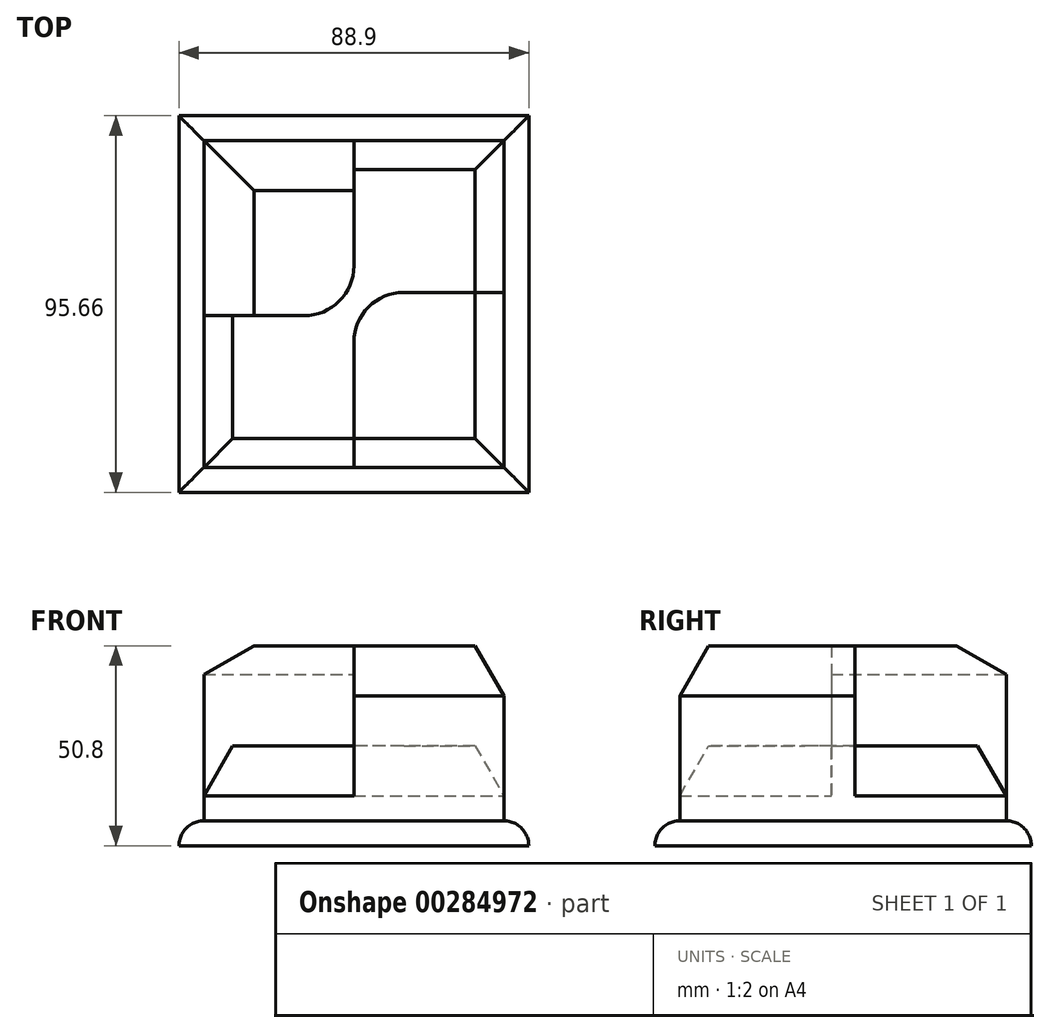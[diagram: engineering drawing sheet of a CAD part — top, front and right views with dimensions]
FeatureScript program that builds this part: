
annotation { "Feature Type Name" : "Feature", "Feature Type Description" : "" }
export const myFeature = defineFeature(function(context is Context, id is Id, definition is map)
    precondition{}
    {
        {
            var Q0;
            Q0=qCreatedBy(makeId("Top.planeOp"),FACE);
            var sketch = newSketch(context, id + "F0", { "sketchPlane" : qUnion([Q0])});
            skLineSegment(sketch, "E0.bottom", {"start": v(44.45, 47.83) * mm, "end": v(-44.45, 47.83) * mm});
            skLineSegment(sketch, "E0.top", {"start": v(44.45, -47.83) * mm, "end": v(-44.45, -47.83) * mm});
            skLineSegment(sketch, "E0.left", {"start": v(44.45, 47.83) * mm, "end": v(44.45, -47.83) * mm});
            skLineSegment(sketch, "E0.right", {"start": v(-44.45, 47.83) * mm, "end": v(-44.45, -47.83) * mm});
            skPoint(sketch, "E0.middle", {"position": v(0, 0) * mm});
            skLineSegment(sketch, "E1.0", {"start": v(38.1, 41.48) * mm, "end": v(-38.1, 41.48) * mm});
            skLineSegment(sketch, "E2.0", {"start": v(38.1, 41.48) * mm, "end": v(38.1, -41.48) * mm});
            skLineSegment(sketch, "E3.0", {"start": v(38.1, -41.48) * mm, "end": v(-38.1, -41.48) * mm});
            skLineSegment(sketch, "E4.0", {"start": v(-38.1, 41.48) * mm, "end": v(-38.1, -41.48) * mm});
            skLineSegment(sketch, "E5", {"start": v(0, 41.48) * mm, "end": v(0, 9.73) * mm});
            skLineSegment(sketch, "E6", {"start": v(-12.7, -2.97) * mm, "end": v(-38.1, -2.97) * mm});
            skLineSegment(sketch, "E7", {"start": v(0, -41.48) * mm, "end": v(0, -9.73) * mm});
            skLineSegment(sketch, "E8", {"start": v(12.7, 2.97) * mm, "end": v(38.1, 2.97) * mm});
            skPoint(sketch, "E9.visualSharp", {"position": v(0, -2.97) * mm});
            skArc(sketch, "E9.filletArc", {"start": v(-12.7, -2.97) * mm, "mid": v(-3.72, 0.75) * mm, "end": v(0, 9.73) * mm});
            skPoint(sketch, "E10.visualSharp", {"position": v(0, 2.97) * mm});
            skArc(sketch, "E10.filletArc", {"start": v(12.7, 2.97) * mm, "mid": v(3.72, -0.75) * mm, "end": v(0, -9.73) * mm});
            skSolve(sketch);
        }
        {
            var Q0;
            Q0=makeQuery(id+"F0.imprint","IMPRINT",FACE,{"disambiguationData":[TD([[makeQuery(id+"F0.imprint","IMPRINT",EDGE,{"derivedFrom":sQuery(id+"F0.wireOp",EDGE,"E0.bottom")}),1.0]])]});
            extrude(context, id + "F1", {"entities" : qUnion([Q0]), "depth" : 6.35 * mm});
        }
        {
            var Q0;
            {var subQ9=sQuery(id+"F0.wireOp",EDGE,"E5");Q0=makeQuery(id+"F0.imprint","IMPRINT",FACE,{"disambiguationData":[TD([[makeQuery(id+"F0.imprint","IMPRINT",EDGE,{"derivedFrom":subQ9}),1.0]])]});}
            extrude(context, id + "F2", {"entities" : qUnion([Q0]), "operationType" : NewBodyOperationType.ADD, "depth" : 25.4 * mm});
        }
        {
            var Q0;
            {var subQ1=sQuery(id+"F0.wireOp",EDGE,"E5");Q0=makeQuery(id+"F0.imprint","IMPRINT",FACE,{"disambiguationData":[TD([[makeQuery(id+"F0.imprint","IMPRINT",EDGE,{"derivedFrom":subQ1}),-1.0]])]});}
            var Q1;
            {var subQ1=sQuery(id+"F0.wireOp",EDGE,"E7");Q1=makeQuery(id+"F0.imprint","IMPRINT",FACE,{"disambiguationData":[TD([[makeQuery(id+"F0.imprint","IMPRINT",EDGE,{"derivedFrom":subQ1}),-1.0]])]});}
            extrude(context, id + "F3", {"entities" : qUnion([Q0, Q1]), "operationType" : NewBodyOperationType.ADD, "depth" : 50.8 * mm});
        }
        {
            var Q0;
            Q0=makeQuery(id+"F1.opExtrude","CAP_EDGE",EDGE,{"disambiguationData":[OSD([sQuery(id+"F0.wireOp",EDGE,"E0.left")])],"isStart":false});
            var Q1;
            Q1=makeQuery(id+"F1.opExtrude","CAP_EDGE",EDGE,{"disambiguationData":[OSD([sQuery(id+"F0.wireOp",EDGE,"E0.top")])],"isStart":false});
            var Q2;
            Q2=makeQuery(id+"F1.opExtrude","CAP_EDGE",EDGE,{"disambiguationData":[OSD([sQuery(id+"F0.wireOp",EDGE,"E0.bottom")])],"isStart":false});
            var Q3;
            Q3=makeQuery(id+"F1.opExtrude","CAP_EDGE",EDGE,{"disambiguationData":[OSD([sQuery(id+"F0.wireOp",EDGE,"E0.right")])],"isStart":false});
            fillet(context, id + "F4", {"entities" : qUnion([Q0, Q1, Q2, Q3]), "radius" : 6.35 * mm, "tangentPropagation" : true, "allowEdgeOverflow" : false});
        }
        {
            var Q0;
            Q0=makeQuery(id+"F2.opExtrude","CAP_EDGE",EDGE,{"disambiguationData":[OSD([sQuery(id+"F0.wireOp",EDGE,"E2.0")])],"isStart":false});
            var Q1;
            Q1=makeQuery(id+"F2.opExtrude","CAP_EDGE",EDGE,{"disambiguationData":[OSD([sQuery(id+"F0.wireOp",EDGE,"E1.0")])],"isStart":false});
            var Q2;
            Q2=makeQuery(id+"F2.opExtrude","CAP_EDGE",EDGE,{"disambiguationData":[OSD([sQuery(id+"F0.wireOp",EDGE,"E4.0")])],"isStart":false});
            var Q3;
            Q3=makeQuery(id+"F2.opExtrude","CAP_EDGE",EDGE,{"disambiguationData":[OSD([sQuery(id+"F0.wireOp",EDGE,"E3.0")])],"isStart":false});
            chamfer(context, id + "F5", {"entities" : qUnion([Q0, Q1, Q2, Q3]), "chamferType" : ChamferType.OFFSET_ANGLE, "width" : 12.7 * mm, "oppositeDirection" : false, "angle" : 30 * degree, "tangentPropagation" : true});
        }
        {
            var Q0;
            Q0=makeQuery(id+"F3.opExtrude","CAP_EDGE",EDGE,{"disambiguationData":[OSD([sQuery(id+"F0.wireOp",EDGE,"E2.0")])],"isStart":false});
            var Q1;
            Q1=makeQuery(id+"F3.opExtrude","CAP_EDGE",EDGE,{"disambiguationData":[OSD([sQuery(id+"F0.wireOp",EDGE,"E3.0")])],"isStart":false});
            var Q2;
            Q2=makeQuery(id+"F3.opExtrude","CAP_EDGE",EDGE,{"disambiguationData":[OSD([sQuery(id+"F0.wireOp",EDGE,"E1.0")])],"isStart":false});
            var Q3;
            Q3=makeQuery(id+"F3.opExtrude","CAP_EDGE",EDGE,{"disambiguationData":[OSD([sQuery(id+"F0.wireOp",EDGE,"E4.0")])],"isStart":false});
            chamfer(context, id + "F6", {"entities" : qUnion([Q0, Q1, Q2, Q3]), "chamferType" : ChamferType.OFFSET_ANGLE, "width" : 12.7 * mm, "oppositeDirection" : false, "angle" : 30 * degree, "tangentPropagation" : true});
        }
    });
